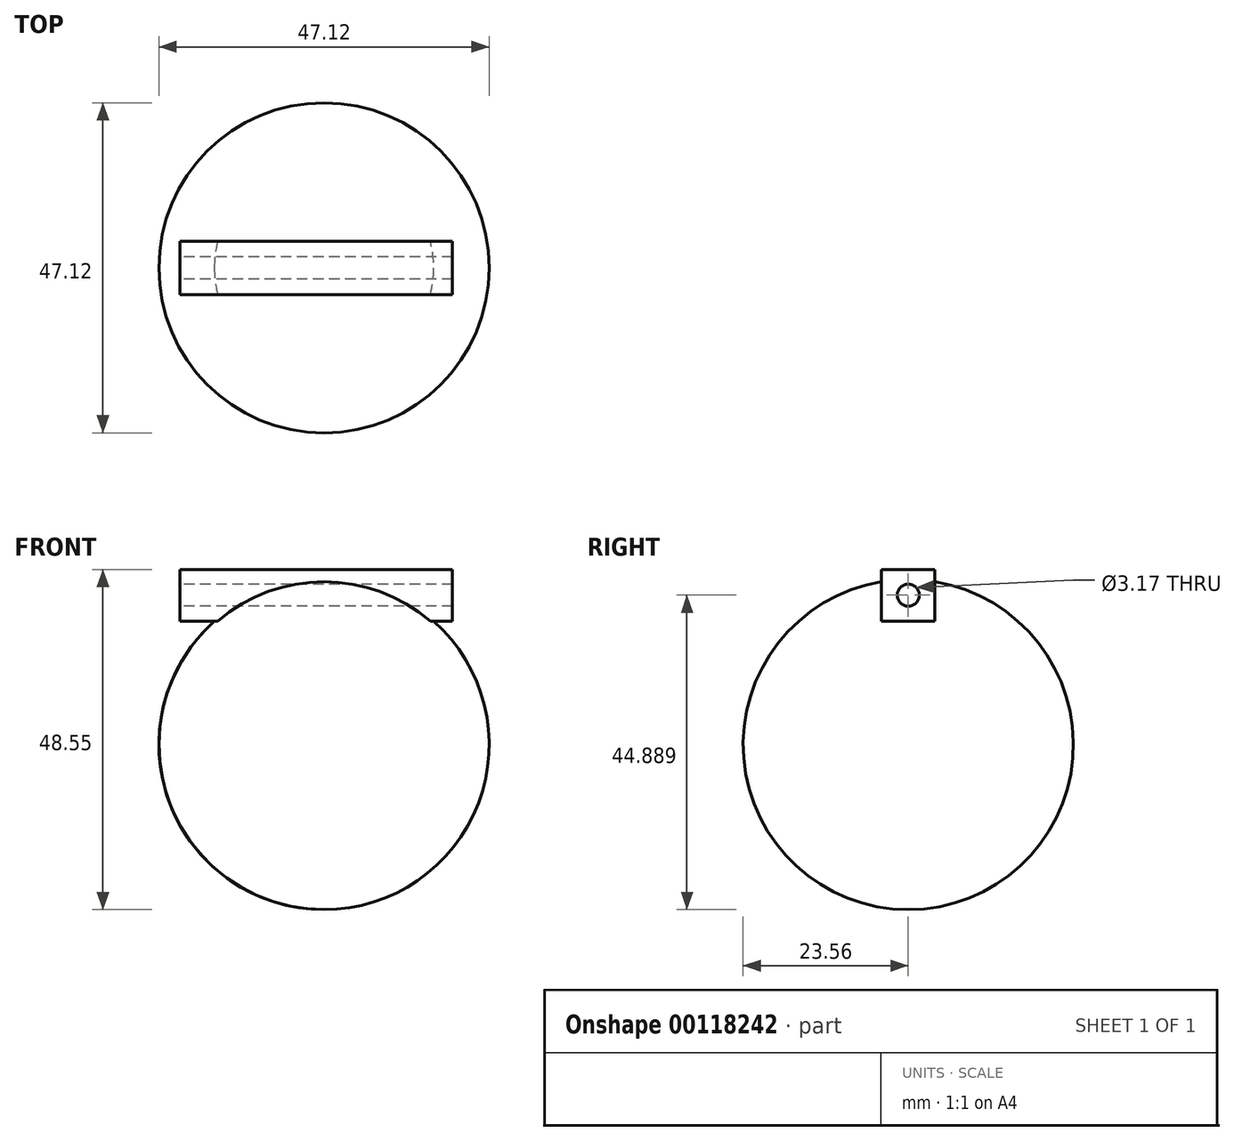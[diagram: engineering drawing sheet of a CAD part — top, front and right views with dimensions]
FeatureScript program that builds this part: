
annotation { "Feature Type Name" : "Feature", "Feature Type Description" : "" }
export const myFeature = defineFeature(function(context is Context, id is Id, definition is map)
    precondition{}
    {
        {
            var Q0;
            Q0=qCreatedBy(makeId("Front.planeOp"),FACE);
            var sketch = newSketch(context, id + "F0", { "sketchPlane" : qUnion([Q0])});
            skLineSegment(sketch, "E0", {"start": v(0, 0) * mm, "end": v(0, 47.12) * mm});
            skArc(sketch, "E1", {"start": v(0, 0) * mm, "mid": v(23.56, 23.56) * mm, "end": v(0, 47.12) * mm});
            skSolve(sketch);
        }
        {
            var Q0;
            Q0=makeQuery(id+"F0.imprint","IMPRINT",FACE,{"disambiguationData":[TD([[makeQuery(id+"F0.imprint","IMPRINT",EDGE,{"derivedFrom":sQuery(id+"F0.wireOp",EDGE,"E0")}),-1.0]])]});
            var Q1;
            Q1=sQuery(id+"F0.wireOp",EDGE,"E0");
            revolve(context, id + "F1", {"entities" : qUnion([Q0]), "axis" : qUnion([Q1]), "revolveType" : RevolveType.FULL});
        }
        {
            var Q0;
            Q0=qCreatedBy(makeId("Front.planeOp"),FACE);
            var sketch = newSketch(context, id + "F2", { "sketchPlane" : qUnion([Q0])});
            skLineSegment(sketch, "E2.bottom", {"start": v(18.33, 48.55) * mm, "end": v(-20.57, 48.55) * mm});
            skLineSegment(sketch, "E2.top", {"start": v(18.33, 41.17) * mm, "end": v(-20.57, 41.17) * mm});
            skLineSegment(sketch, "E2.left", {"start": v(18.33, 48.55) * mm, "end": v(18.33, 41.17) * mm});
            skLineSegment(sketch, "E2.right", {"start": v(-20.57, 48.55) * mm, "end": v(-20.57, 41.17) * mm});
            skSolve(sketch);
        }
        {
            var Q0;
            Q0=makeQuery(id+"F2.imprint","IMPRINT",FACE,{"disambiguationData":[TD([[makeQuery(id+"F2.imprint","IMPRINT",EDGE,{"derivedFrom":sQuery(id+"F2.wireOp",EDGE,"E2.bottom")}),1.0]])]});
            extrude(context, id + "F3", {"entities" : qUnion([Q0]), "operationType" : NewBodyOperationType.ADD, "endBound" : BoundingType.SYMMETRIC, "depth" : 7.62 * mm});
        }
        {
            var Q0;
            Q0=qCreatedBy(makeId("Right.planeOp"),FACE);
            var sketch = newSketch(context, id + "F4", { "sketchPlane" : qUnion([Q0])});
            skCircle(sketch, "E3", {"center": v(0, 44.89) * mm, "radius": 1.58 * mm});
            skSolve(sketch);
        }
        {
            var Q0;
            Q0 = qSketchRegion(id + "F4", true);
            extrude(context, id + "F5", {"entities" : qUnion([Q0]), "operationType" : NewBodyOperationType.REMOVE, "endBound" : BoundingType.SYMMETRIC, "depth" : 45.72 * mm});
        }
    });
